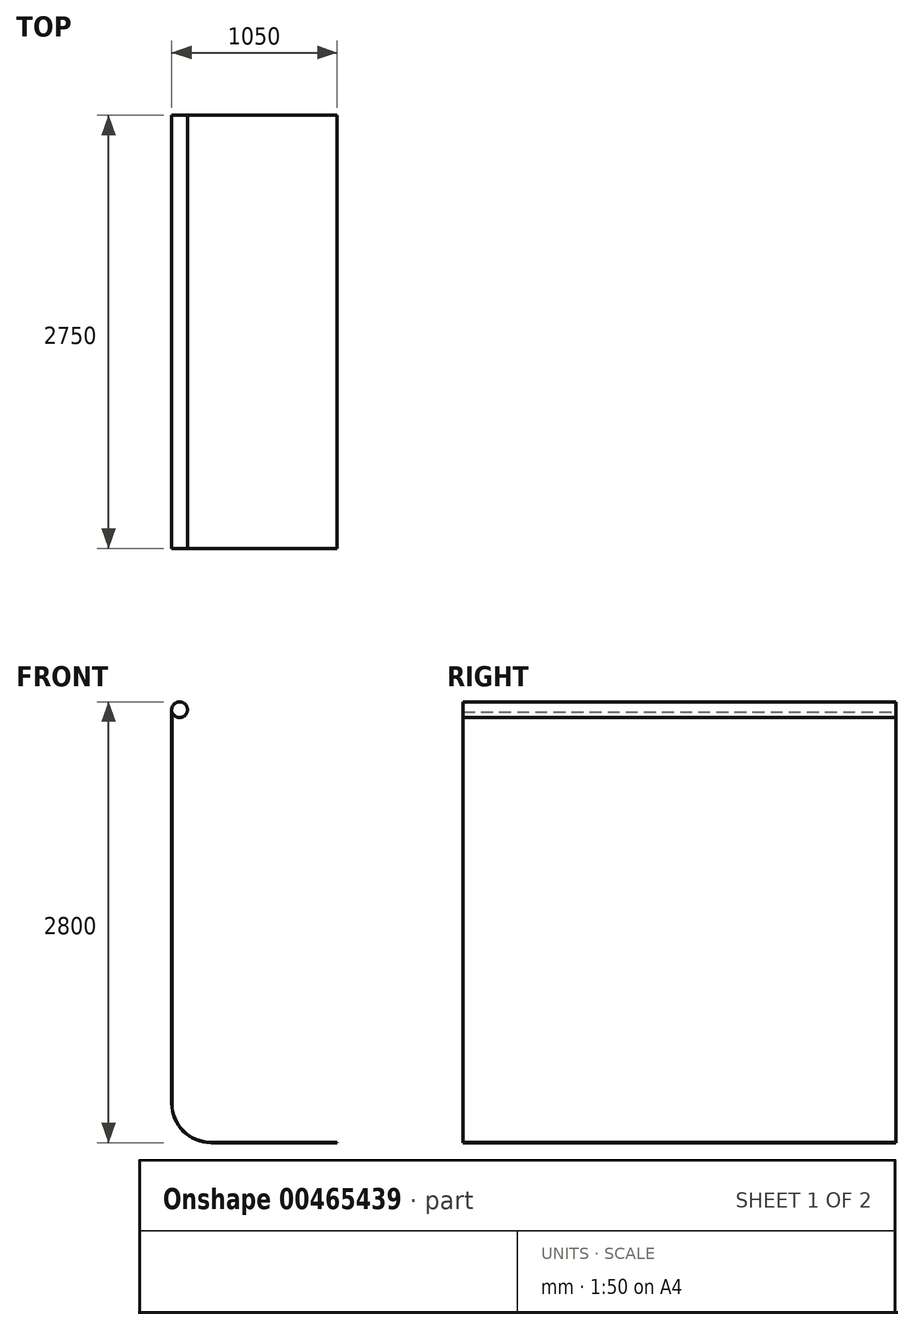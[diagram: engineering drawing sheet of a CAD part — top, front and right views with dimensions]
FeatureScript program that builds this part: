
annotation { "Feature Type Name" : "Feature", "Feature Type Description" : "" }
export const myFeature = defineFeature(function(context is Context, id is Id, definition is map)
    precondition{}
    {
        {
            var Q0;
            Q0=qCreatedBy(makeId("Front.planeOp"),FACE);
            var sketch = newSketch(context, id + "F0", { "sketchPlane" : qUnion([Q0])});
            skArc(sketch, "E0", {"start": v(-48, -14) * mm, "mid": v(49.5, 7.07) * mm, "end": v(-50, 0) * mm});
            skLineSegment(sketch, "E1", {"start": v(-50, 0) * mm, "end": v(-50, -2500) * mm});
            skArc(sketch, "E2", {"start": v(-50, -2500) * mm, "mid": v(23.22, -2676.78) * mm, "end": v(200, -2750) * mm});
            skLineSegment(sketch, "E3", {"start": v(200, -2750) * mm, "end": v(1000, -2750) * mm});
            skLineSegment(sketch, "E4", {"start": v(1000, -2750) * mm, "end": v(1000, -2748) * mm});
            skLineSegment(sketch, "E5", {"start": v(1000, -2748) * mm, "end": v(200, -2748) * mm});
            skArc(sketch, "E6", {"start": v(200, -2748) * mm, "mid": v(24.64, -2675.36) * mm, "end": v(-48, -2500) * mm});
            skLineSegment(sketch, "E7", {"start": v(-48, -2500) * mm, "end": v(-48, -14) * mm});
            skSolve(sketch);
        }
        {
            var Q0;
            Q0 = qSketchRegion(id + "F0", true);
            extrude(context, id + "F1", {"entities" : qUnion([Q0]), "depth" : 2750 * mm});
        }
    });
